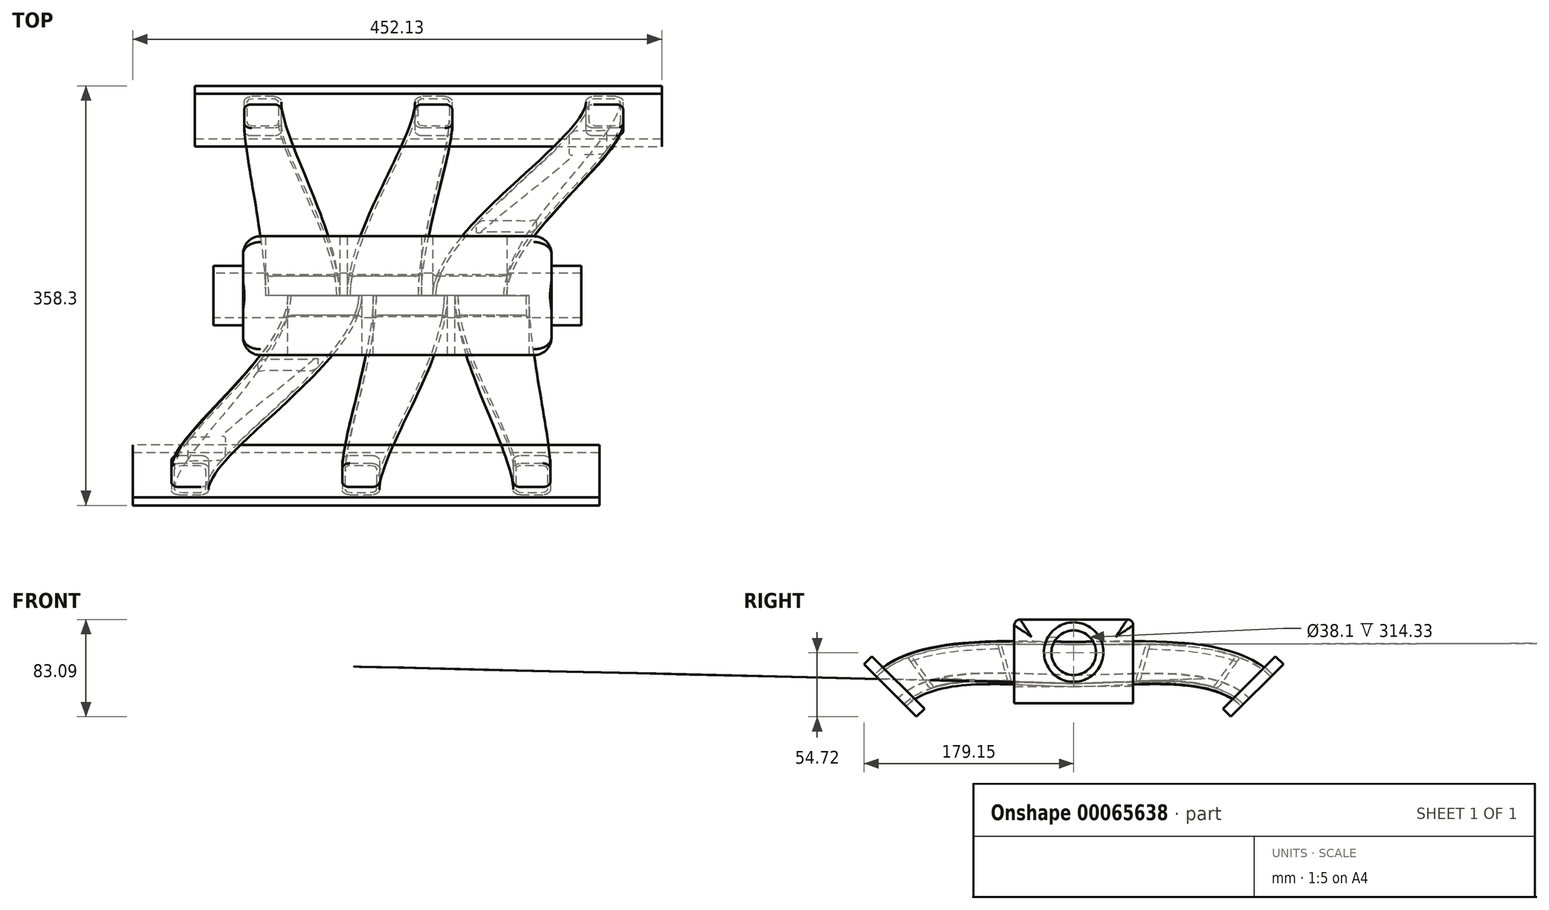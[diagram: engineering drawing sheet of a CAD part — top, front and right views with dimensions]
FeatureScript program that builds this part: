
annotation { "Feature Type Name" : "Feature", "Feature Type Description" : "" }
export const myFeature = defineFeature(function(context is Context, id is Id, definition is map)
    precondition{}
    {
        {
            var Q0;
            Q0=qCreatedBy(makeId("Front.planeOp"),FACE);
            var sketch = newSketch(context, id + "F0", { "sketchPlane" : qUnion([Q0])});
            skLineSegment(sketch, "E0.bottom", {"start": v(-143.83, 301.55) * mm, "end": v(119.7, 301.55) * mm});
            skLineSegment(sketch, "E0.top", {"start": v(-143.83, 230.08) * mm, "end": v(119.7, 230.08) * mm});
            skLineSegment(sketch, "E0.left", {"start": v(-143.83, 301.55) * mm, "end": v(-143.83, 230.08) * mm});
            skLineSegment(sketch, "E0.right", {"start": v(119.7, 301.55) * mm, "end": v(119.7, 230.08) * mm});
            skLineSegment(sketch, "E1.bottom", {"start": v(43.5, 282.5) * mm, "end": v(94.3, 282.5) * mm});
            skLineSegment(sketch, "E1.top", {"start": v(43.5, 244.4) * mm, "end": v(94.3, 244.4) * mm});
            skLineSegment(sketch, "E1.left", {"start": v(37.15, 276.15) * mm, "end": v(37.15, 250.75) * mm});
            skLineSegment(sketch, "E1.right", {"start": v(100.65, 276.15) * mm, "end": v(100.65, 250.75) * mm});
            skPoint(sketch, "E2.visualSharp", {"position": v(37.15, 282.5) * mm});
            skArc(sketch, "E2.filletArc", {"start": v(43.5, 282.5) * mm, "mid": v(39, 280.64) * mm, "end": v(37.15, 276.15) * mm});
            skPoint(sketch, "E3.visualSharp", {"position": v(100.65, 282.5) * mm});
            skArc(sketch, "E3.filletArc", {"start": v(100.65, 276.15) * mm, "mid": v(98.8, 280.64) * mm, "end": v(94.3, 282.5) * mm});
            skPoint(sketch, "E4.visualSharp", {"position": v(100.65, 244.4) * mm});
            skArc(sketch, "E4.filletArc", {"start": v(94.3, 244.4) * mm, "mid": v(98.8, 246.26) * mm, "end": v(100.65, 250.75) * mm});
            skPoint(sketch, "E5.visualSharp", {"position": v(37.15, 244.4) * mm});
            skArc(sketch, "E5.filletArc", {"start": v(37.15, 250.75) * mm, "mid": v(39, 246.26) * mm, "end": v(43.5, 244.4) * mm});
            skLineSegment(sketch, "E6.1.0.0", {"start": v(-26.35, 282.5) * mm, "end": v(24.45, 282.5) * mm});
            skArc(sketch, "E6.1.0.1", {"start": v(-26.35, 282.5) * mm, "mid": v(-30.84, 280.64) * mm, "end": v(-32.7, 276.15) * mm});
            skLineSegment(sketch, "E6.1.0.2", {"start": v(-32.7, 276.15) * mm, "end": v(-32.7, 250.75) * mm});
            skArc(sketch, "E6.1.0.3", {"start": v(-32.7, 250.75) * mm, "mid": v(-30.84, 246.26) * mm, "end": v(-26.35, 244.4) * mm});
            skLineSegment(sketch, "E6.1.0.4", {"start": v(-26.35, 244.4) * mm, "end": v(24.45, 244.4) * mm});
            skArc(sketch, "E6.1.0.5", {"start": v(24.45, 244.4) * mm, "mid": v(28.94, 246.26) * mm, "end": v(30.8, 250.75) * mm});
            skLineSegment(sketch, "E6.1.0.6", {"start": v(30.8, 276.15) * mm, "end": v(30.8, 250.75) * mm});
            skArc(sketch, "E6.1.0.7", {"start": v(30.8, 276.15) * mm, "mid": v(28.94, 280.64) * mm, "end": v(24.45, 282.5) * mm});
            skLineSegment(sketch, "E6.direction1", {"start": v(43.5, 282.5) * mm, "end": v(-26.35, 282.5) * mm, "construction": true});
            skLineSegment(sketch, "E7.1.0.0", {"start": v(-105.73, 276.15) * mm, "end": v(-105.73, 250.75) * mm});
            skLineSegment(sketch, "E7.1.0.1", {"start": v(-99.38, 282.5) * mm, "end": v(-48.58, 282.5) * mm});
            skArc(sketch, "E7.1.0.2", {"start": v(-99.38, 282.5) * mm, "mid": v(-103.87, 280.64) * mm, "end": v(-105.73, 276.15) * mm});
            skArc(sketch, "E7.1.0.3", {"start": v(-105.73, 250.75) * mm, "mid": v(-103.87, 246.26) * mm, "end": v(-99.38, 244.4) * mm});
            skLineSegment(sketch, "E7.1.0.4", {"start": v(-99.38, 244.4) * mm, "end": v(-48.58, 244.4) * mm});
            skArc(sketch, "E7.1.0.5", {"start": v(-48.58, 244.4) * mm, "mid": v(-44.09, 246.26) * mm, "end": v(-42.23, 250.75) * mm});
            skLineSegment(sketch, "E7.1.0.6", {"start": v(-42.23, 276.15) * mm, "end": v(-42.23, 250.75) * mm});
            skArc(sketch, "E7.1.0.7", {"start": v(-42.23, 276.15) * mm, "mid": v(-44.09, 280.64) * mm, "end": v(-48.58, 282.5) * mm});
            skLineSegment(sketch, "E7.direction1", {"start": v(37.15, 250.75) * mm, "end": v(-105.73, 250.75) * mm, "construction": true});
            skSolve(sketch);
        }
        {
            var Q0;
            Q0=qCreatedBy(makeId("Front.planeOp"),FACE);
            var Q1;
            Q1=qCreatedBy(makeId("Top.planeOp"),FACE);
            cPlane(context, id + "F1", {"entities" : qUnion([Q0, Q1]), "cplaneType" : CPlaneType.MID_PLANE, "offset" : 152.4 * mm, "width" : 152.4 * mm, "height" : 152.4 * mm});
        }
        {
            var Q0;
            Q0=qCreatedBy(id+"F1.planeOp",FACE);
            cPlane(context, id + "F2", {"entities" : qUnion([Q0]), "cplaneType" : CPlaneType.OFFSET, "offset" : 59.55 * mm, "oppositeDirection" : true, "width" : 152.4 * mm, "height" : 152.4 * mm});
        }
        {
            var Q0;
            Q0=qCreatedBy(id+"F2.planeOp",FACE);
            var sketch = newSketch(context, id + "F3", { "sketchPlane" : qUnion([Q0])});
            skLineSegment(sketch, "E8.bottom", {"start": v(160.76, 312.9) * mm, "end": v(-238.13, 312.9) * mm});
            skLineSegment(sketch, "E8.top", {"start": v(160.76, 249.4) * mm, "end": v(-238.13, 249.4) * mm});
            skLineSegment(sketch, "E8.left", {"start": v(160.76, 312.9) * mm, "end": v(160.76, 249.4) * mm});
            skLineSegment(sketch, "E8.right", {"start": v(-238.13, 312.9) * mm, "end": v(-238.13, 249.4) * mm});
            skLineSegment(sketch, "E9.rect.bottom", {"start": v(-198.76, 262.1) * mm, "end": v(-179.71, 262.1) * mm});
            skLineSegment(sketch, "E9.rect.top", {"start": v(-198.76, 300.2) * mm, "end": v(-179.71, 300.2) * mm});
            skLineSegment(sketch, "E9.rect.left", {"start": v(-205.11, 268.45) * mm, "end": v(-205.11, 293.85) * mm});
            skLineSegment(sketch, "E9.rect.right", {"start": v(-173.36, 268.45) * mm, "end": v(-173.36, 293.85) * mm});
            skPoint(sketch, "E9.rect.middle", {"position": v(-189.24, 281.15) * mm});
            skLineSegment(sketch, "E10", {"start": v(-238.13, 281.15) * mm, "end": v(160.76, 281.15) * mm, "construction": true});
            skPoint(sketch, "E11.visualSharp", {"position": v(-173.36, 300.2) * mm});
            skArc(sketch, "E11.filletArc", {"start": v(-173.36, 293.85) * mm, "mid": v(-175.22, 298.34) * mm, "end": v(-179.71, 300.2) * mm});
            skPoint(sketch, "E12.visualSharp", {"position": v(-205.11, 300.2) * mm});
            skArc(sketch, "E12.filletArc", {"start": v(-198.76, 300.2) * mm, "mid": v(-203.25, 298.34) * mm, "end": v(-205.11, 293.85) * mm});
            skPoint(sketch, "E13.visualSharp", {"position": v(-173.36, 262.1) * mm});
            skArc(sketch, "E13.filletArc", {"start": v(-179.71, 262.1) * mm, "mid": v(-175.22, 263.96) * mm, "end": v(-173.36, 268.45) * mm});
            skPoint(sketch, "E14.visualSharp", {"position": v(-205.11, 262.1) * mm});
            skArc(sketch, "E14.filletArc", {"start": v(-205.11, 268.45) * mm, "mid": v(-203.25, 263.96) * mm, "end": v(-198.76, 262.1) * mm});
            skLineSegment(sketch, "E15.1.0.0", {"start": v(-52.71, 262.1) * mm, "end": v(-33.66, 262.1) * mm});
            skArc(sketch, "E15.1.0.1", {"start": v(-33.66, 262.1) * mm, "mid": v(-29.17, 263.96) * mm, "end": v(-27.31, 268.45) * mm});
            skLineSegment(sketch, "E15.1.0.2", {"start": v(-27.31, 268.45) * mm, "end": v(-27.31, 293.85) * mm});
            skArc(sketch, "E15.1.0.3", {"start": v(-27.31, 293.85) * mm, "mid": v(-29.17, 298.34) * mm, "end": v(-33.66, 300.2) * mm});
            skLineSegment(sketch, "E15.1.0.4", {"start": v(-52.71, 300.2) * mm, "end": v(-33.66, 300.2) * mm});
            skArc(sketch, "E15.1.0.5", {"start": v(-52.71, 300.2) * mm, "mid": v(-57.2, 298.34) * mm, "end": v(-59.06, 293.85) * mm});
            skLineSegment(sketch, "E15.1.0.6", {"start": v(-59.06, 268.45) * mm, "end": v(-59.06, 293.85) * mm});
            skArc(sketch, "E15.1.0.7", {"start": v(-59.06, 268.45) * mm, "mid": v(-57.2, 263.96) * mm, "end": v(-52.71, 262.1) * mm});
            skLineSegment(sketch, "E15.2.0.0", {"start": v(93.34, 262.1) * mm, "end": v(112.39, 262.1) * mm});
            skArc(sketch, "E15.2.0.1", {"start": v(112.39, 262.1) * mm, "mid": v(116.88, 263.96) * mm, "end": v(118.74, 268.45) * mm});
            skLineSegment(sketch, "E15.2.0.2", {"start": v(118.74, 268.45) * mm, "end": v(118.74, 293.85) * mm});
            skArc(sketch, "E15.2.0.3", {"start": v(118.74, 293.85) * mm, "mid": v(116.88, 298.34) * mm, "end": v(112.39, 300.2) * mm});
            skLineSegment(sketch, "E15.2.0.4", {"start": v(93.34, 300.2) * mm, "end": v(112.39, 300.2) * mm});
            skArc(sketch, "E15.2.0.5", {"start": v(93.34, 300.2) * mm, "mid": v(88.85, 298.34) * mm, "end": v(86.99, 293.85) * mm});
            skLineSegment(sketch, "E15.2.0.6", {"start": v(86.99, 268.45) * mm, "end": v(86.99, 293.85) * mm});
            skArc(sketch, "E15.2.0.7", {"start": v(86.99, 268.45) * mm, "mid": v(88.85, 263.96) * mm, "end": v(93.34, 262.1) * mm});
            skLineSegment(sketch, "E15.direction1", {"start": v(-198.76, 262.1) * mm, "end": v(-52.71, 262.1) * mm, "construction": true});
            skSolve(sketch);
        }
        {
            var Q0;
            Q0=makeQuery(id+"F0.imprint","IMPRINT",FACE,{"disambiguationData":[TD([[makeQuery(id+"F0.imprint","IMPRINT",EDGE,{"derivedFrom":sQuery(id+"F0.wireOp",EDGE,"E7.1.0.0")}),1.0]])]});
            var Q1;
            Q1=makeQuery(id+"F3.imprint","IMPRINT",FACE,{"disambiguationData":[TD([[makeQuery(id+"F3.imprint","IMPRINT",EDGE,{"derivedFrom":sQuery(id+"F3.wireOp",EDGE,"E9.rect.bottom")}),1.0]])]});
            loft(context, id + "F4", {"startCondition" : LoftEndDerivativeType.NORMAL_TO_PROFILE, "startMagnitude" : 1, "endCondition" : LoftEndDerivativeType.NORMAL_TO_PROFILE, "endMagnitude" : 1, "sheetProfilesArray" : [{ "sheetProfileEntities" : qUnion([Q0]) }, { "sheetProfileEntities" : qUnion([Q1]) }]});
        }
        {
            var Q0;
            Q0=makeQuery(id+"F0.imprint","IMPRINT",FACE,{"disambiguationData":[TD([[makeQuery(id+"F0.imprint","IMPRINT",EDGE,{"derivedFrom":sQuery(id+"F0.wireOp",EDGE,"E6.1.0.0")}),-1.0]])]});
            var Q1;
            Q1=makeQuery(id+"F3.imprint","IMPRINT",FACE,{"disambiguationData":[TD([[makeQuery(id+"F3.imprint","IMPRINT",EDGE,{"derivedFrom":sQuery(id+"F3.wireOp",EDGE,"E15.1.0.0")}),1.0]])]});
            loft(context, id + "F5", {"startCondition" : LoftEndDerivativeType.NORMAL_TO_PROFILE, "startMagnitude" : 1, "endCondition" : LoftEndDerivativeType.NORMAL_TO_PROFILE, "endMagnitude" : 1, "sheetProfilesArray" : [{ "sheetProfileEntities" : qUnion([Q0]) }, { "sheetProfileEntities" : qUnion([Q1]) }]});
        }
        {
            var Q0;
            Q0=makeQuery(id+"F0.imprint","IMPRINT",FACE,{"disambiguationData":[TD([[makeQuery(id+"F0.imprint","IMPRINT",EDGE,{"derivedFrom":sQuery(id+"F0.wireOp",EDGE,"E1.bottom")}),-1.0]])]});
            var Q1;
            Q1=makeQuery(id+"F3.imprint","IMPRINT",FACE,{"disambiguationData":[TD([[makeQuery(id+"F3.imprint","IMPRINT",EDGE,{"derivedFrom":sQuery(id+"F3.wireOp",EDGE,"E15.2.0.0")}),1.0]])]});
            loft(context, id + "F6", {"startCondition" : LoftEndDerivativeType.NORMAL_TO_PROFILE, "startMagnitude" : 1, "endCondition" : LoftEndDerivativeType.NORMAL_TO_PROFILE, "endMagnitude" : 1, "sheetProfilesArray" : [{ "sheetProfileEntities" : qUnion([Q0]) }, { "sheetProfileEntities" : qUnion([Q1]) }]});
        }
        {
            var Q0;
            Q0 = qSketchRegion(id + "F0", true);
            extrude(context, id + "F7", {"entities" : qUnion([Q0]), "depth" : 50.8 * mm});
        }
        {
            var Q0;
            Q0=makeQuery(id+"F4.opLoft","CAP_FACE",FACE,{"disambiguationData":[OSD([makeQuery(id+"F3.imprint","IMPRINT",FACE,{"disambiguationData":[TD([[makeQuery(id+"F3.imprint","IMPRINT",EDGE,{"derivedFrom":sQuery(id+"F3.wireOp",EDGE,"E9.rect.bottom")}),1.0]])]})])],"isStart":true});
            var Q1;
            Q1=makeQuery(id+"F4.opLoft","CAP_FACE",FACE,{"disambiguationData":[OSD([makeQuery(id+"F0.imprint","IMPRINT",FACE,{"disambiguationData":[TD([[makeQuery(id+"F0.imprint","IMPRINT",EDGE,{"derivedFrom":sQuery(id+"F0.wireOp",EDGE,"E7.1.0.0")}),1.0]])]})])],"isStart":true});
            shell(context, id + "F8", {"entities" : qUnion([Q0, Q1]), "thickness" : 2.54 * mm});
        }
        {
            var Q0;
            Q0=makeQuery(id+"F5.opLoft","CAP_FACE",FACE,{"disambiguationData":[OSD([makeQuery(id+"F0.imprint","IMPRINT",FACE,{"disambiguationData":[TD([[makeQuery(id+"F0.imprint","IMPRINT",EDGE,{"derivedFrom":sQuery(id+"F0.wireOp",EDGE,"E6.1.0.0")}),-1.0]])]})])],"isStart":true});
            var Q1;
            Q1=makeQuery(id+"F5.opLoft","CAP_FACE",FACE,{"disambiguationData":[OSD([makeQuery(id+"F3.imprint","IMPRINT",FACE,{"disambiguationData":[TD([[makeQuery(id+"F3.imprint","IMPRINT",EDGE,{"derivedFrom":sQuery(id+"F3.wireOp",EDGE,"E15.1.0.0")}),1.0]])]})])],"isStart":true});
            var Q2;
            Q2=makeQuery(id+"F5.opLoft","SWEPT_BODY",BODY,{"disambiguationData":[OSD([makeQuery(id+"F0.imprint","IMPRINT",FACE,{"disambiguationData":[TD([[makeQuery(id+"F0.imprint","IMPRINT",EDGE,{"derivedFrom":sQuery(id+"F0.wireOp",EDGE,"E6.1.0.0")}),-1.0]])]}),makeQuery(id+"F3.imprint","IMPRINT",FACE,{"disambiguationData":[TD([[makeQuery(id+"F3.imprint","IMPRINT",EDGE,{"derivedFrom":sQuery(id+"F3.wireOp",EDGE,"E15.1.0.0")}),1.0]])]})])]});
            shell(context, id + "F9", {"entities" : qUnion([Q0, Q1]), "parts" : qUnion([Q2]), "thickness" : 2.54 * mm});
        }
        {
            var Q0;
            Q0=makeQuery(id+"F6.opLoft","CAP_FACE",FACE,{"disambiguationData":[OSD([makeQuery(id+"F0.imprint","IMPRINT",FACE,{"disambiguationData":[TD([[makeQuery(id+"F0.imprint","IMPRINT",EDGE,{"derivedFrom":sQuery(id+"F0.wireOp",EDGE,"E1.bottom")}),-1.0]])]})])],"isStart":true});
            var Q1;
            Q1=makeQuery(id+"F6.opLoft","CAP_FACE",FACE,{"disambiguationData":[OSD([makeQuery(id+"F3.imprint","IMPRINT",FACE,{"disambiguationData":[TD([[makeQuery(id+"F3.imprint","IMPRINT",EDGE,{"derivedFrom":sQuery(id+"F3.wireOp",EDGE,"E15.2.0.0")}),1.0]])]})])],"isStart":true});
            shell(context, id + "F10", {"entities" : qUnion([Q0, Q1]), "thickness" : 2.54 * mm});
        }
        {
            var Q0;
            Q0 = qSketchRegion(id + "F3", true);
            extrude(context, id + "F11", {"entities" : qUnion([Q0]), "oppositeDirection" : true, "depth" : 9.52 * mm});
        }
        {
            var Q0;
            Q0=makeQuery(id+"F7.opExtrude","CAP_EDGE",EDGE,{"disambiguationData":[OSD([sQuery(id+"F0.wireOp",EDGE,"E0.bottom")])],"isStart":false});
            fillet(context, id + "F12", {"entities" : qUnion([Q0]), "radius" : 5 * mm, "tangentPropagation" : true, "allowEdgeOverflow" : false});
        }
        {
            var Q0;
            Q0=makeQuery(id+"F7.opExtrude","SWEPT_EDGE",EDGE,{"disambiguationData":[OSD([sQuery(id+"F0.wireOp",EDGE,"E0.bottom"),sQuery(id+"F0.wireOp",EDGE,"E0.right")])]});
            fillet(context, id + "F13", {"entities" : qUnion([Q0]), "radius" : 15 * mm, "tangentPropagation" : true, "allowEdgeOverflow" : false});
        }
        {
            var Q0;
            Q0=makeQuery(id+"F7.opExtrude","SWEPT_EDGE",EDGE,{"disambiguationData":[OSD([sQuery(id+"F0.wireOp",EDGE,"E0.bottom"),sQuery(id+"F0.wireOp",EDGE,"E0.left")])]});
            fillet(context, id + "F14", {"entities" : qUnion([Q0]), "radius" : 15 * mm, "tangentPropagation" : true, "allowEdgeOverflow" : false});
        }
        {
            var Q0;
            Q0=makeQuery(id+"F7.opExtrude","CAP_FACE",FACE,{"disambiguationData":[OSD([sQuery(id+"F0.wireOp",EDGE,"E0.bottom"),sQuery(id+"F0.wireOp",EDGE,"E0.top"),sQuery(id+"F0.wireOp",EDGE,"E0.left"),sQuery(id+"F0.wireOp",EDGE,"E0.right"),sQuery(id+"F0.wireOp",EDGE,"E1.bottom"),sQuery(id+"F0.wireOp",EDGE,"E1.top"),sQuery(id+"F0.wireOp",EDGE,"E1.left"),sQuery(id+"F0.wireOp",EDGE,"E1.right"),sQuery(id+"F0.wireOp",EDGE,"E2.filletArc"),sQuery(id+"F0.wireOp",EDGE,"E3.filletArc"),sQuery(id+"F0.wireOp",EDGE,"E4.filletArc"),sQuery(id+"F0.wireOp",EDGE,"E5.filletArc"),sQuery(id+"F0.wireOp",EDGE,"E6.1.0.0"),sQuery(id+"F0.wireOp",EDGE,"E6.1.0.1"),sQuery(id+"F0.wireOp",EDGE,"E6.1.0.2"),sQuery(id+"F0.wireOp",EDGE,"E6.1.0.3"),sQuery(id+"F0.wireOp",EDGE,"E6.1.0.4"),sQuery(id+"F0.wireOp",EDGE,"E6.1.0.5"),sQuery(id+"F0.wireOp",EDGE,"E6.1.0.6"),sQuery(id+"F0.wireOp",EDGE,"E6.1.0.7"),sQuery(id+"F0.wireOp",EDGE,"E7.1.0.0"),sQuery(id+"F0.wireOp",EDGE,"E7.1.0.1"),sQuery(id+"F0.wireOp",EDGE,"E7.1.0.2"),sQuery(id+"F0.wireOp",EDGE,"E7.1.0.3"),sQuery(id+"F0.wireOp",EDGE,"E7.1.0.4"),sQuery(id+"F0.wireOp",EDGE,"E7.1.0.5"),sQuery(id+"F0.wireOp",EDGE,"E7.1.0.6"),sQuery(id+"F0.wireOp",EDGE,"E7.1.0.7")])],"isStart":true});
            var sketch = newSketch(context, id + "F15", { "sketchPlane" : qUnion([Q0])});
            skLineSegment(sketch, "E16", {"start": v(12.07, 301.55) * mm, "end": v(12.07, 230.08) * mm, "construction": true});
            skSolve(sketch);
        }
        {
            var Q0;
            Q0=makeQuery(id+"F11.opExtrude","SWEPT_BODY",BODY,{"disambiguationData":[OSD([sQuery(id+"F3.wireOp",EDGE,"E8.bottom"),sQuery(id+"F3.wireOp",EDGE,"E8.top"),sQuery(id+"F3.wireOp",EDGE,"E8.left"),sQuery(id+"F3.wireOp",EDGE,"E8.right"),sQuery(id+"F3.wireOp",EDGE,"E9.rect.bottom"),sQuery(id+"F3.wireOp",EDGE,"E9.rect.top"),sQuery(id+"F3.wireOp",EDGE,"E9.rect.left"),sQuery(id+"F3.wireOp",EDGE,"E9.rect.right"),sQuery(id+"F3.wireOp",EDGE,"E11.filletArc"),sQuery(id+"F3.wireOp",EDGE,"E12.filletArc"),sQuery(id+"F3.wireOp",EDGE,"E13.filletArc"),sQuery(id+"F3.wireOp",EDGE,"E14.filletArc"),sQuery(id+"F3.wireOp",EDGE,"E15.1.0.0"),sQuery(id+"F3.wireOp",EDGE,"E15.1.0.1"),sQuery(id+"F3.wireOp",EDGE,"E15.1.0.2"),sQuery(id+"F3.wireOp",EDGE,"E15.1.0.3"),sQuery(id+"F3.wireOp",EDGE,"E15.1.0.4"),sQuery(id+"F3.wireOp",EDGE,"E15.1.0.5"),sQuery(id+"F3.wireOp",EDGE,"E15.1.0.6"),sQuery(id+"F3.wireOp",EDGE,"E15.1.0.7"),sQuery(id+"F3.wireOp",EDGE,"E15.2.0.0"),sQuery(id+"F3.wireOp",EDGE,"E15.2.0.1"),sQuery(id+"F3.wireOp",EDGE,"E15.2.0.2"),sQuery(id+"F3.wireOp",EDGE,"E15.2.0.3"),sQuery(id+"F3.wireOp",EDGE,"E15.2.0.4"),sQuery(id+"F3.wireOp",EDGE,"E15.2.0.5"),sQuery(id+"F3.wireOp",EDGE,"E15.2.0.6"),sQuery(id+"F3.wireOp",EDGE,"E15.2.0.7")])]});
            var Q1;
            Q1=makeQuery(id+"F6.opLoft","SWEPT_BODY",BODY,{"disambiguationData":[OSD([makeQuery(id+"F0.imprint","IMPRINT",FACE,{"disambiguationData":[TD([[makeQuery(id+"F0.imprint","IMPRINT",EDGE,{"derivedFrom":sQuery(id+"F0.wireOp",EDGE,"E1.bottom")}),-1.0]])]}),makeQuery(id+"F3.imprint","IMPRINT",FACE,{"disambiguationData":[TD([[makeQuery(id+"F3.imprint","IMPRINT",EDGE,{"derivedFrom":sQuery(id+"F3.wireOp",EDGE,"E15.2.0.0")}),1.0]])]})])]});
            var Q2;
            Q2=makeQuery(id+"F5.opLoft","SWEPT_BODY",BODY,{"disambiguationData":[OSD([makeQuery(id+"F0.imprint","IMPRINT",FACE,{"disambiguationData":[TD([[makeQuery(id+"F0.imprint","IMPRINT",EDGE,{"derivedFrom":sQuery(id+"F0.wireOp",EDGE,"E6.1.0.0")}),-1.0]])]}),makeQuery(id+"F3.imprint","IMPRINT",FACE,{"disambiguationData":[TD([[makeQuery(id+"F3.imprint","IMPRINT",EDGE,{"derivedFrom":sQuery(id+"F3.wireOp",EDGE,"E15.1.0.0")}),1.0]])]})])]});
            var Q3;
            Q3=makeQuery(id+"F4.opLoft","SWEPT_BODY",BODY,{"disambiguationData":[OSD([makeQuery(id+"F0.imprint","IMPRINT",FACE,{"disambiguationData":[TD([[makeQuery(id+"F0.imprint","IMPRINT",EDGE,{"derivedFrom":sQuery(id+"F0.wireOp",EDGE,"E7.1.0.0")}),1.0]])]}),makeQuery(id+"F3.imprint","IMPRINT",FACE,{"disambiguationData":[TD([[makeQuery(id+"F3.imprint","IMPRINT",EDGE,{"derivedFrom":sQuery(id+"F3.wireOp",EDGE,"E9.rect.bottom")}),1.0]])]})])]});
            var Q4;
            Q4=makeQuery(id+"F7.opExtrude","SWEPT_BODY",BODY,{"disambiguationData":[OSD([sQuery(id+"F0.wireOp",EDGE,"E0.bottom"),sQuery(id+"F0.wireOp",EDGE,"E0.top"),sQuery(id+"F0.wireOp",EDGE,"E0.left"),sQuery(id+"F0.wireOp",EDGE,"E0.right"),sQuery(id+"F0.wireOp",EDGE,"E1.bottom"),sQuery(id+"F0.wireOp",EDGE,"E1.top"),sQuery(id+"F0.wireOp",EDGE,"E1.left"),sQuery(id+"F0.wireOp",EDGE,"E1.right"),sQuery(id+"F0.wireOp",EDGE,"E2.filletArc"),sQuery(id+"F0.wireOp",EDGE,"E3.filletArc"),sQuery(id+"F0.wireOp",EDGE,"E4.filletArc"),sQuery(id+"F0.wireOp",EDGE,"E5.filletArc"),sQuery(id+"F0.wireOp",EDGE,"E6.1.0.0"),sQuery(id+"F0.wireOp",EDGE,"E6.1.0.1"),sQuery(id+"F0.wireOp",EDGE,"E6.1.0.2"),sQuery(id+"F0.wireOp",EDGE,"E6.1.0.3"),sQuery(id+"F0.wireOp",EDGE,"E6.1.0.4"),sQuery(id+"F0.wireOp",EDGE,"E6.1.0.5"),sQuery(id+"F0.wireOp",EDGE,"E6.1.0.6"),sQuery(id+"F0.wireOp",EDGE,"E6.1.0.7"),sQuery(id+"F0.wireOp",EDGE,"E7.1.0.0"),sQuery(id+"F0.wireOp",EDGE,"E7.1.0.1"),sQuery(id+"F0.wireOp",EDGE,"E7.1.0.2"),sQuery(id+"F0.wireOp",EDGE,"E7.1.0.3"),sQuery(id+"F0.wireOp",EDGE,"E7.1.0.4"),sQuery(id+"F0.wireOp",EDGE,"E7.1.0.5"),sQuery(id+"F0.wireOp",EDGE,"E7.1.0.6"),sQuery(id+"F0.wireOp",EDGE,"E7.1.0.7")])]});
            var Q5;
            Q5=sQuery(id+"F15.wireOp",EDGE,"E16");
            circularPattern(context, id + "F16", {"entities" : qUnion([Q0, Q1, Q2, Q3, Q4]), "axis" : qUnion([Q5]), "angle" : 180 * degree, "instanceCount" : 2, "equalSpace" : true});
        }
        {
            var Q0;
            Q0=makeQuery(id+"F16.opPattern","COPY",FACE,{"derivedFrom":makeQuery(id+"F7.opExtrude","SWEPT_FACE",FACE,{"disambiguationData":[OSD([sQuery(id+"F0.wireOp",EDGE,"E0.left")])]}),"instanceName":"1"});
            var sketch = newSketch(context, id + "F17", { "sketchPlane" : qUnion([Q0])});
            skCircle(sketch, "E17", {"center": v(0, 273.68) * mm, "radius": 25.4 * mm});
            skSolve(sketch);
        }
        {
            var Q0;
            Q0=makeQuery(id+"F7.opExtrude","SWEPT_FACE",FACE,{"disambiguationData":[OSD([sQuery(id+"F0.wireOp",EDGE,"E0.left")])]});
            var sketch = newSketch(context, id + "F18", { "sketchPlane" : qUnion([Q0])});
            skCircle(sketch, "E18", {"center": v(0, 273.18) * mm, "radius": 25.4 * mm});
            skSolve(sketch);
        }
        {
            var Q0;
            Q0 = qSketchRegion(id + "F17", true);
            extrude(context, id + "F19", {"entities" : qUnion([Q0]), "operationType" : NewBodyOperationType.ADD, "depth" : 25.4 * mm});
        }
        {
            var Q0;
            Q0 = qSketchRegion(id + "F18", true);
            extrude(context, id + "F20", {"entities" : qUnion([Q0]), "operationType" : NewBodyOperationType.ADD, "depth" : 25.4 * mm});
        }
        {
            var Q0;
            Q0=makeQuery(id+"F20.opExtrude","CAP_FACE",FACE,{"disambiguationData":[OSD([sQuery(id+"F18.wireOp",EDGE,"E18")])],"isStart":false});
            var sketch = newSketch(context, id + "F21", { "sketchPlane" : qUnion([Q0])});
            skCircle(sketch, "E19", {"center": v(0, 273.18) * mm, "radius": 19.05 * mm});
            skSolve(sketch);
        }
        {
            var Q0;
            Q0=makeQuery(id+"F21.imprint","IMPRINT",FACE,{"disambiguationData":[TD([[makeQuery(id+"F21.imprint","IMPRINT",EDGE,{"derivedFrom":sQuery(id+"F21.wireOp",EDGE,"E19")}),1.0]])]});
            extrude(context, id + "F22", {"entities" : qUnion([Q0]), "operationType" : NewBodyOperationType.REMOVE, "endBound" : BoundingType.THROUGH_ALL, "oppositeDirection" : true, "depth" : 25.4 * mm});
        }
    });
